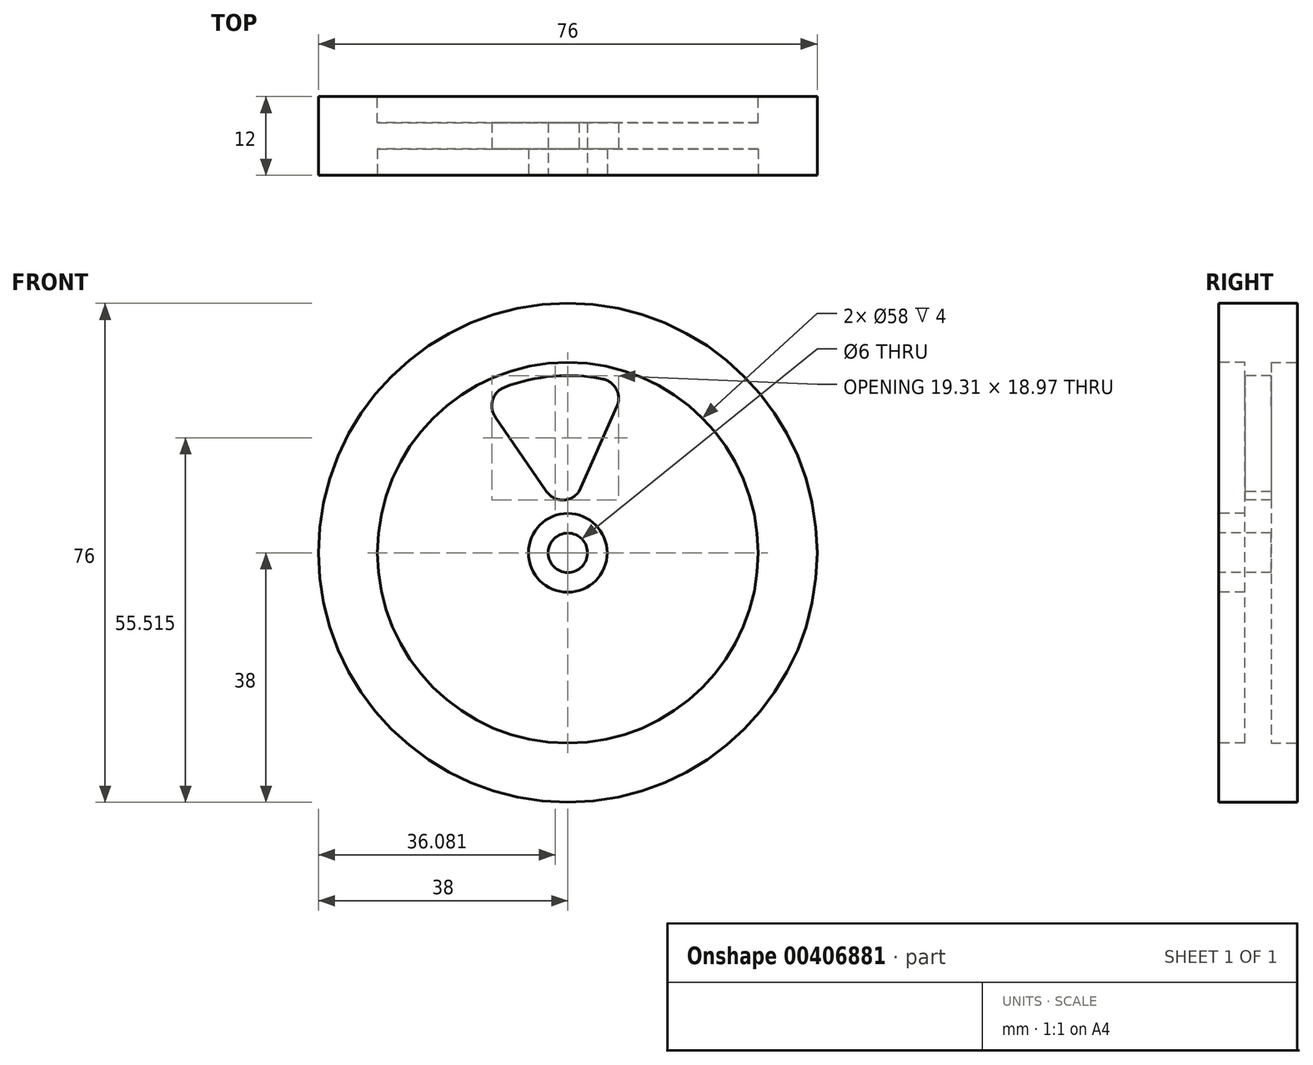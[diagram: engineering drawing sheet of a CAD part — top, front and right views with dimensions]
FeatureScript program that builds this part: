
annotation { "Feature Type Name" : "Feature", "Feature Type Description" : "" }
export const myFeature = defineFeature(function(context is Context, id is Id, definition is map)
    precondition{}
    {
        {
            var Q0;
            Q0=qCreatedBy(makeId("Front.planeOp"),FACE);
            var sketch = newSketch(context, id + "F0", { "sketchPlane" : qUnion([Q0])});
            skCircle(sketch, "E0", {"center": v(0, 0) * mm, "radius": 38 * mm});
            skSolve(sketch);
        }
        {
            var Q0;
            Q0=makeQuery(id+"F0.imprint","IMPRINT",FACE,{"disambiguationData":[TD([[makeQuery(id+"F0.imprint","IMPRINT",EDGE,{"derivedFrom":sQuery(id+"F0.wireOp",EDGE,"E0")}),1.0]])]});
            extrude(context, id + "F1", {"entities" : qUnion([Q0]), "endBound" : BoundingType.SYMMETRIC, "depth" : 12 * mm});
        }
        {
            var Q0;
            Q0=makeQuery(id+"F1.opExtrude","CAP_FACE",FACE,{"disambiguationData":[OSD([sQuery(id+"F0.wireOp",EDGE,"E0")])],"isStart":false});
            var sketch = newSketch(context, id + "F2", { "sketchPlane" : qUnion([Q0])});
            skCircle(sketch, "E1", {"center": v(0, 0) * mm, "radius": 3 * mm});
            skCircle(sketch, "E2", {"center": v(0, 0) * mm, "radius": 6 * mm});
            skCircle(sketch, "E3", {"center": v(0, 0) * mm, "radius": 29 * mm});
            skSolve(sketch);
        }
        {
            var Q0;
            Q0=makeQuery(id+"F2.imprint","IMPRINT",FACE,{"disambiguationData":[TD([[makeQuery(id+"F2.imprint","IMPRINT",EDGE,{"derivedFrom":sQuery(id+"F2.wireOp",EDGE,"E1")}),1.0]])]});
            extrude(context, id + "F3", {"entities" : qUnion([Q0]), "operationType" : NewBodyOperationType.REMOVE, "oppositeDirection" : true, "depth" : 25 * mm});
        }
        {
            var Q0;
            Q0=makeQuery(id+"F2.imprint","IMPRINT",FACE,{"disambiguationData":[TD([[makeQuery(id+"F2.imprint","IMPRINT",EDGE,{"derivedFrom":sQuery(id+"F2.wireOp",EDGE,"E2")}),-1.0]])]});
            extrude(context, id + "F4", {"entities" : qUnion([Q0]), "operationType" : NewBodyOperationType.REMOVE, "oppositeDirection" : true, "depth" : 4 * mm});
        }
        {
            var Q0;
            Q0=makeQuery(id+"F2.imprint","IMPRINT",FACE,{"disambiguationData":[TD([[makeQuery(id+"F2.imprint","IMPRINT",EDGE,{"derivedFrom":sQuery(id+"F2.wireOp",EDGE,"E2")}),-1.0]])]});
            var sketch = newSketch(context, id + "F5", { "sketchPlane" : qUnion([Q0])});
            skCircle(sketch, "E4", {"center": v(0, 0) * mm, "radius": 27 * mm});
            skLineSegment(sketch, "E5", {"start": v(-13.06, 23.63) * mm, "end": v(-3.23, 9.33) * mm});
            skLineSegment(sketch, "E6", {"start": v(8.9, 25.5) * mm, "end": v(1.71, 9.33) * mm});
            skArc(sketch, "E7", {"start": v(-3.23, 9.33) * mm, "mid": v(-0.76, 8.03) * mm, "end": v(1.71, 9.33) * mm});
            skSolve(sketch);
        }
        {
            var Q0;
            {var subQ0=sQuery(id+"F5.wireOp",EDGE,"E5");Q0=makeQuery(id+"F5.imprint","IMPRINT",FACE,{"disambiguationData":[TD([[makeQuery(id+"F5.imprint","IMPRINT",EDGE,{"derivedFrom":subQ0}),1.0]])]});}
            extrude(context, id + "F6", {"entities" : qUnion([Q0]), "operationType" : NewBodyOperationType.REMOVE, "oppositeDirection" : true, "depth" : 25 * mm});
        }
        {
            var Q0;
            Q0=makeQuery(id+"F6.boolean.opBoolean","COPY",EDGE,{"derivedFrom":makeQuery(id+"F6.opExtrude","SWEPT_EDGE",EDGE,{"disambiguationData":[OSD([sQuery(id+"F5.wireOp",EDGE,"E4"),sQuery(id+"F5.wireOp",EDGE,"E5")])]})});
            var Q1;
            Q1=makeQuery(id+"F6.boolean.opBoolean","COPY",EDGE,{"derivedFrom":makeQuery(id+"F6.opExtrude","SWEPT_EDGE",EDGE,{"disambiguationData":[OSD([sQuery(id+"F5.wireOp",EDGE,"E4"),sQuery(id+"F5.wireOp",EDGE,"E6")])]})});
            fillet(context, id + "F7", {"entities" : qUnion([Q0, Q1]), "radius" : 3 * mm, "tangentPropagation" : true, "allowEdgeOverflow" : false});
        }
        {
            var Q0;
            Q0=makeQuery(id+"F1.opExtrude","CAP_FACE",FACE,{"disambiguationData":[OSD([sQuery(id+"F0.wireOp",EDGE,"E0")])],"isStart":true});
            var sketch = newSketch(context, id + "F8", { "sketchPlane" : qUnion([Q0])});
            skCircle(sketch, "E8.0", {"center": v(0, 0) * mm, "radius": 29 * mm});
            skSolve(sketch);
        }
        {
            var Q0;
            Q0=makeQuery(id+"F8.imprint","IMPRINT",FACE,{"disambiguationData":[TD([[makeQuery(id+"F8.imprint","IMPRINT",EDGE,{"derivedFrom":sQuery(id+"F8.wireOp",EDGE,"E8.0")}),1.0]])]});
            extrude(context, id + "F9", {"entities" : qUnion([Q0]), "operationType" : NewBodyOperationType.REMOVE, "oppositeDirection" : true, "depth" : 4 * mm});
        }
    });
